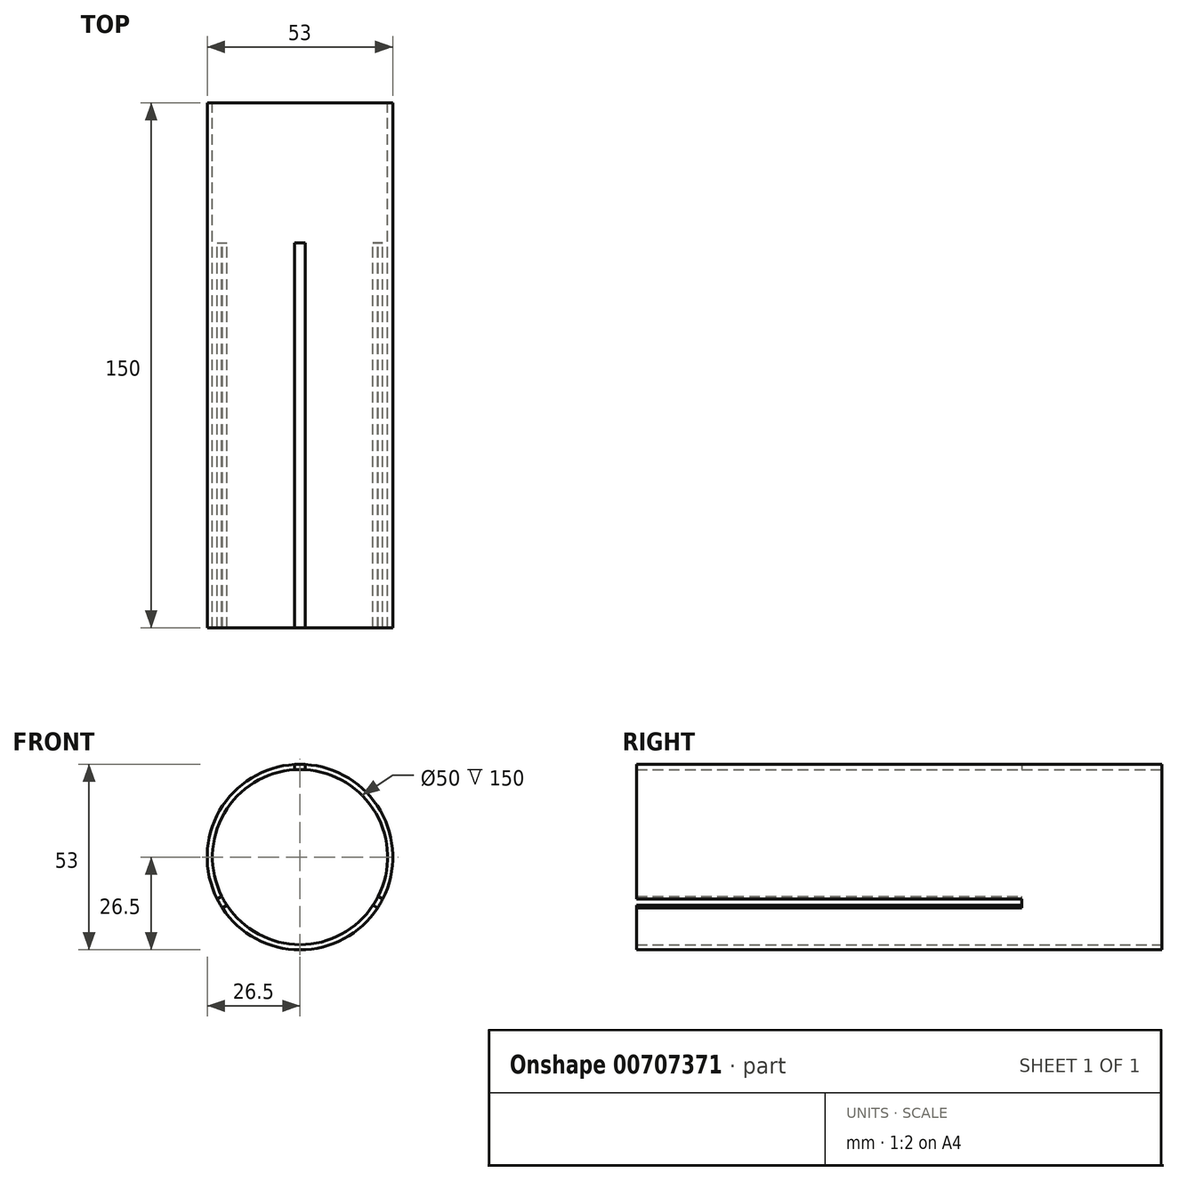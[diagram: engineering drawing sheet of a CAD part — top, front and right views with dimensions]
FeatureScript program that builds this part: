
annotation { "Feature Type Name" : "Feature", "Feature Type Description" : "" }
export const myFeature = defineFeature(function(context is Context, id is Id, definition is map)
    precondition{}
    {
        {
            var Q0;
            Q0=qCreatedBy(makeId("Front.planeOp"),FACE);
            var sketch = newSketch(context, id + "F0", { "sketchPlane" : qUnion([Q0])});
            skCircle(sketch, "E0", {"center": v(0, 0) * mm, "radius": 25 * mm});
            skCircle(sketch, "E1", {"center": v(0, 0) * mm, "radius": 26.5 * mm});
            skSolve(sketch);
        }
        {
            var Q0;
            Q0=makeQuery(id+"F0.imprint","IMPRINT",FACE,{"disambiguationData":[TD([[makeQuery(id+"F0.imprint","IMPRINT",EDGE,{"derivedFrom":sQuery(id+"F0.wireOp",EDGE,"E0")}),-1.0]])]});
            extrude(context, id + "F1", {"entities" : qUnion([Q0]), "endBound" : BoundingType.SYMMETRIC, "depth" : 150 * mm, "offsetDistance" : 25 * mm});
        }
        {
            var Q0;
            Q0=qCreatedBy(makeId("Front.planeOp"),FACE);
            cPlane(context, id + "F2", {"entities" : qUnion([Q0]), "cplaneType" : CPlaneType.OFFSET, "offset" : 75 * mm, "width" : 150 * mm, "height" : 150 * mm});
        }
        {
            var Q0;
            Q0=qCreatedBy(id+"F2.planeOp",FACE);
            var sketch = newSketch(context, id + "F3", { "sketchPlane" : qUnion([Q0])});
            skLineSegment(sketch, "E2.bottom", {"start": v(-1.5, 27) * mm, "end": v(1.5, 27) * mm});
            skLineSegment(sketch, "E2.top", {"start": v(-1.5, 22) * mm, "end": v(1.5, 22) * mm});
            skLineSegment(sketch, "E2.left", {"start": v(-1.5, 27) * mm, "end": v(-1.5, 22) * mm});
            skLineSegment(sketch, "E2.right", {"start": v(1.5, 27) * mm, "end": v(1.5, 22) * mm});
            skLineSegment(sketch, "E3.1.0", {"start": v(-22.63, -14.8) * mm, "end": v(-24.13, -12.2) * mm});
            skLineSegment(sketch, "E3.1.1", {"start": v(-24.13, -12.2) * mm, "end": v(-19.8, -9.7) * mm});
            skLineSegment(sketch, "E3.1.2", {"start": v(-18.3, -12.3) * mm, "end": v(-19.8, -9.7) * mm});
            skLineSegment(sketch, "E3.1.3", {"start": v(-22.63, -14.8) * mm, "end": v(-18.3, -12.3) * mm});
            skLineSegment(sketch, "E3.2.0", {"start": v(24.13, -12.2) * mm, "end": v(22.63, -14.8) * mm});
            skLineSegment(sketch, "E3.2.1", {"start": v(22.63, -14.8) * mm, "end": v(18.3, -12.3) * mm});
            skLineSegment(sketch, "E3.2.2", {"start": v(19.8, -9.7) * mm, "end": v(18.3, -12.3) * mm});
            skLineSegment(sketch, "E3.2.3", {"start": v(24.13, -12.2) * mm, "end": v(19.8, -9.7) * mm});
            skPoint(sketch, "E3.center", {"position": v(0, 0) * mm});
            skSolve(sketch);
        }
        {
            var Q0;
            Q0=makeQuery(id+"F3.imprint","IMPRINT",FACE,{"disambiguationData":[TD([[makeQuery(id+"F3.imprint","IMPRINT",EDGE,{"derivedFrom":sQuery(id+"F3.wireOp",EDGE,"E2.bottom")}),-1.0]])]});
            var Q1;
            Q1=makeQuery(id+"F3.imprint","IMPRINT",FACE,{"disambiguationData":[TD([[makeQuery(id+"F3.imprint","IMPRINT",EDGE,{"derivedFrom":sQuery(id+"F3.wireOp",EDGE,"E3.1.0")}),-1.0]])]});
            var Q2;
            Q2=makeQuery(id+"F3.imprint","IMPRINT",FACE,{"disambiguationData":[TD([[makeQuery(id+"F3.imprint","IMPRINT",EDGE,{"derivedFrom":sQuery(id+"F3.wireOp",EDGE,"E3.2.0")}),-1.0]])]});
            extrude(context, id + "F4", {"entities" : qUnion([Q0, Q1, Q2]), "operationType" : NewBodyOperationType.REMOVE, "oppositeDirection" : true, "depth" : 110 * mm, "offsetDistance" : 25 * mm});
        }
    });
